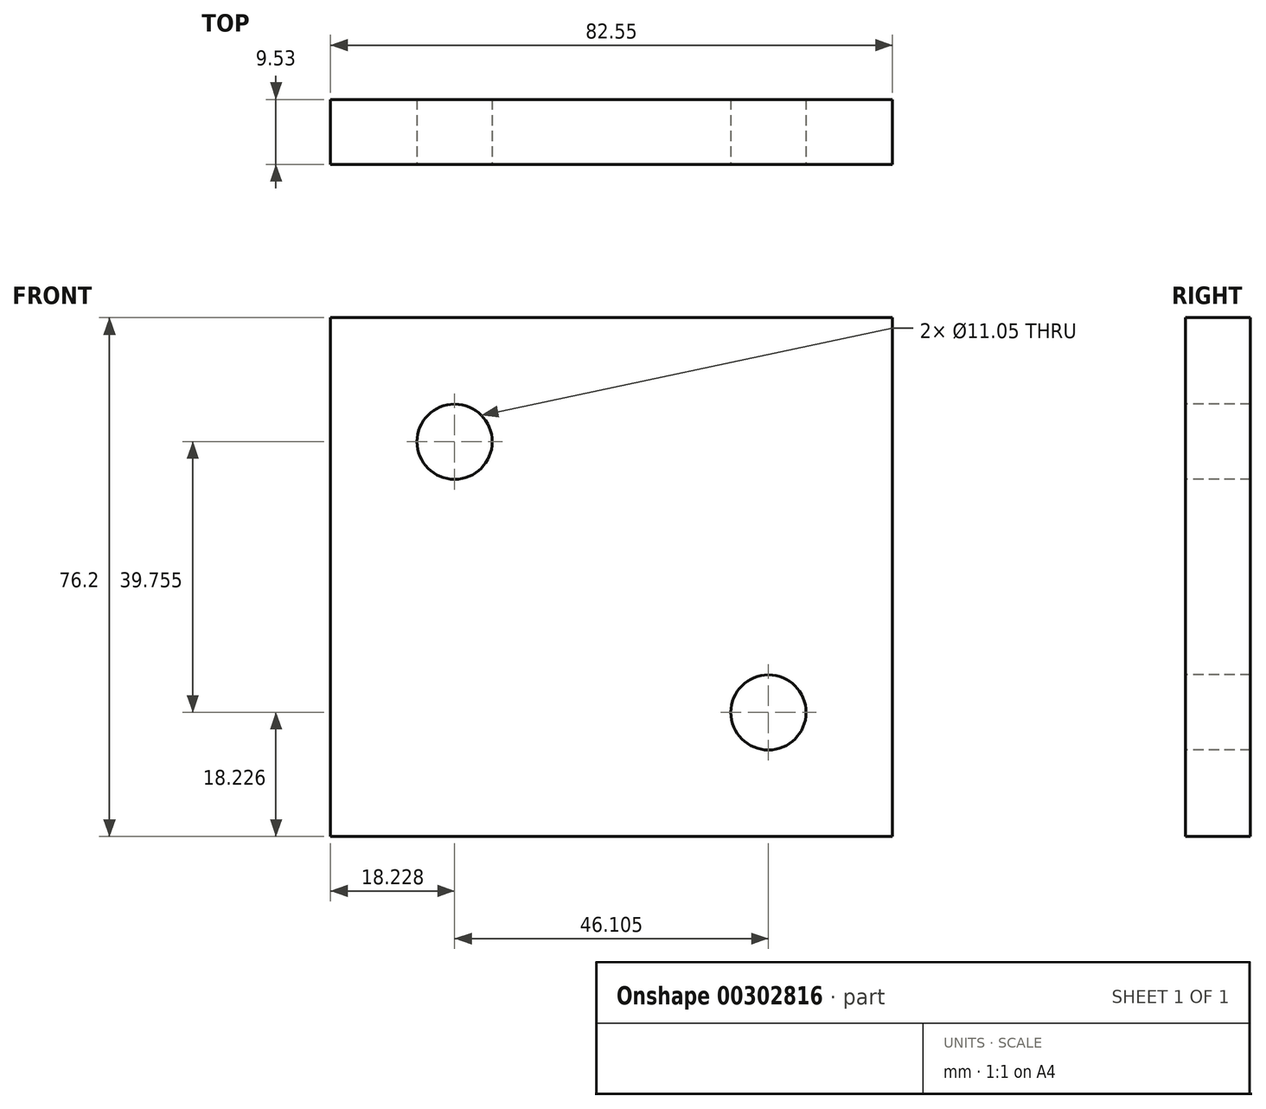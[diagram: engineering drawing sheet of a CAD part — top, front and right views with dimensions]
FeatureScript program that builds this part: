
annotation { "Feature Type Name" : "Feature", "Feature Type Description" : "" }
export const myFeature = defineFeature(function(context is Context, id is Id, definition is map)
    precondition{}
    {
        {
            var Q0;
            Q0=qCreatedBy(makeId("Front.planeOp"),FACE);
            var sketch = newSketch(context, id + "F0", { "sketchPlane" : qUnion([Q0])});
            skLineSegment(sketch, "E0.bottom", {"start": v(-38.47, 68.58) * mm, "end": v(44.08, 68.58) * mm});
            skLineSegment(sketch, "E0.top", {"start": v(-38.47, -7.62) * mm, "end": v(44.08, -7.62) * mm});
            skLineSegment(sketch, "E0.left", {"start": v(-38.47, 68.58) * mm, "end": v(-38.47, -7.62) * mm});
            skLineSegment(sketch, "E0.right", {"start": v(44.08, 68.58) * mm, "end": v(44.08, -7.62) * mm});
            skSolve(sketch);
        }
        {
            var Q0;
            Q0 = qSketchRegion(id + "F0", true);
            extrude(context, id + "F1", {"entities" : qUnion([Q0]), "depth" : 3.17 * mm * 3});
        }
        {
            var Q0;
            Q0=makeQuery(id+"F1.opExtrude","CAP_FACE",FACE,{"disambiguationData":[OSD([sQuery(id+"F0.wireOp",EDGE,"E0.bottom"),sQuery(id+"F0.wireOp",EDGE,"E0.top"),sQuery(id+"F0.wireOp",EDGE,"E0.left"),sQuery(id+"F0.wireOp",EDGE,"E0.right")])],"isStart":false});
            var sketch = newSketch(context, id + "F2", { "sketchPlane" : qUnion([Q0])});
            skCircle(sketch, "E1", {"center": v(-20.24, 50.36) * mm, "radius": 5.52 * mm});
            skCircle(sketch, "E2", {"center": v(25.86, 10.6) * mm, "radius": 5.52 * mm});
            skSolve(sketch);
        }
        {
            var Q0;
            Q0 = qSketchRegion(id + "F2", true);
            extrude(context, id + "F3", {"entities" : qUnion([Q0]), "operationType" : NewBodyOperationType.REMOVE, "endBound" : BoundingType.THROUGH_ALL, "oppositeDirection" : true, "depth" : 25.4 * mm});
        }
    });
